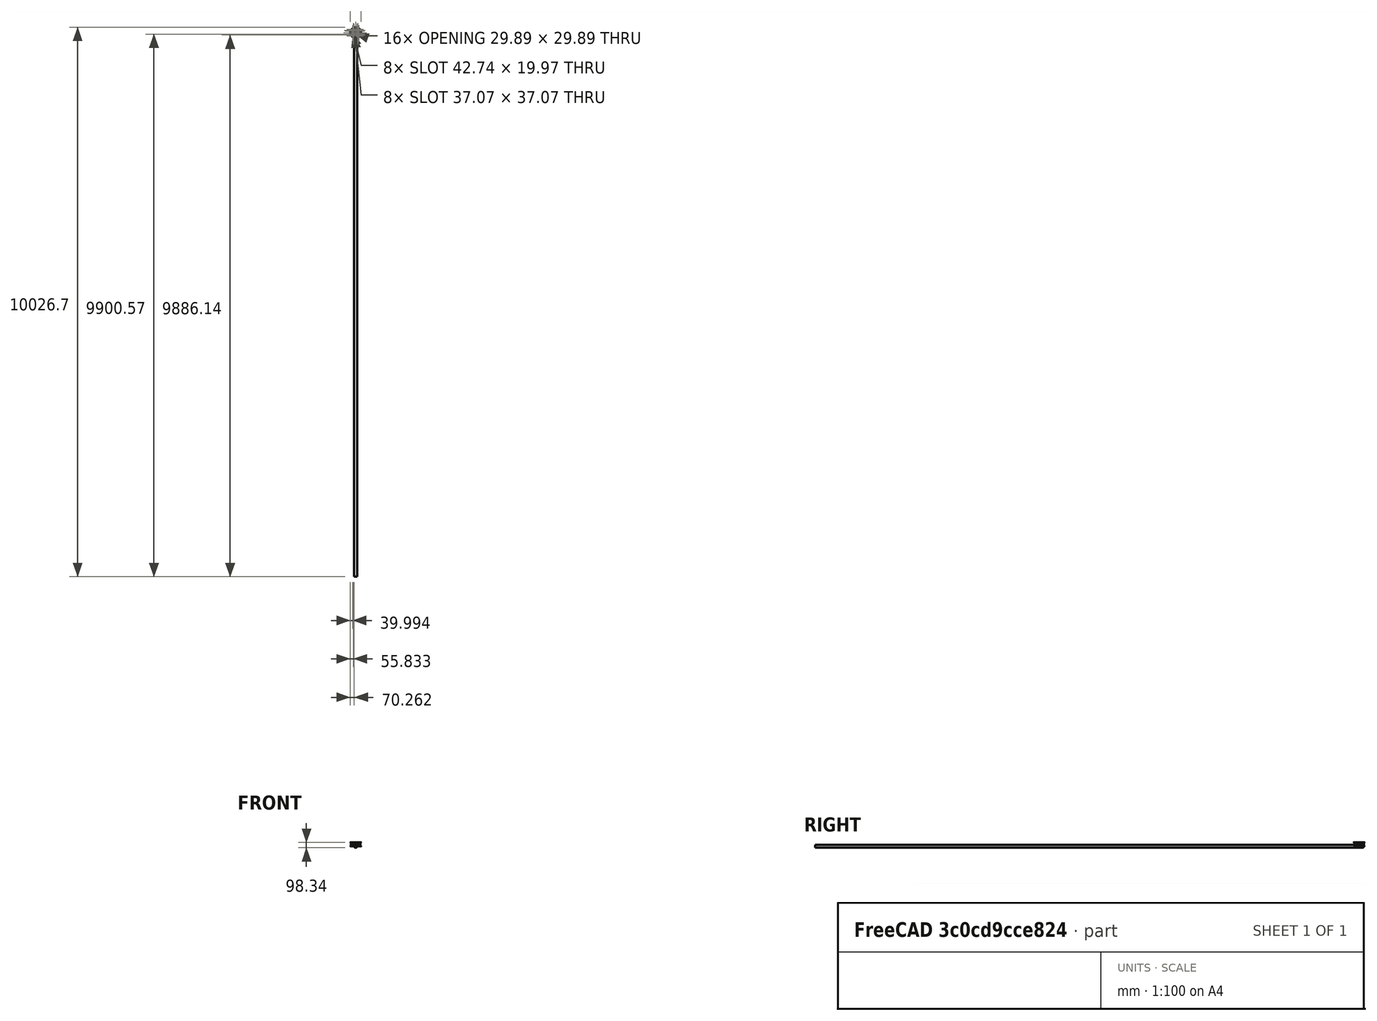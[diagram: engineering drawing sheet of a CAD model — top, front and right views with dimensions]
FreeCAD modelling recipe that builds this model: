
FCSTD DOCUMENT  (FreeCAD 0.14R3702 (Git))
Label: PLA-Reel
License: CC-BY 3.0
LicenseURL: http://creativecommons.org/licenses/by/3.0/
objects: Sketcher::SketchObject×7, PartDesign::Pocket×6, PartDesign::PolarPattern×5, Part::Extrusion×5, Part::Feature×3, Part::Part2DObjectPython×2, Part::MultiFuse×2, PartDesign::Revolution×1, Part::Cylinder×1, Part::Cut×1, Part::Torus×1, Part::FeaturePython×1, Part::Compound×1
note: 43 computed .brp shape members not serialized (recipe doc carries the construction recipe); baked Part::Feature solids carry a one-line shape summary decoded from their .brp

FEATURE [Sketcher::SketchObject] Sketch  label="main-body-sketch"
  Placement = pos=(0,0,0) rot=(1,0,0;1.5708rad)
  sketch-geometry (20):
    g0: LineSegment StartX=0 StartY=71.5 StartZ=0 EndX=97.185 EndY=71.5 EndZ=0
    g1: LineSegment StartX=97.185 StartY=0 StartZ=0 EndX=0 EndY=0 EndZ=0
    g2: LineSegment StartX=0 StartY=0 StartZ=0 EndX=0 EndY=71.5 EndZ=0
    g3: LineSegment [constr] StartX=0 StartY=35.75 StartZ=0 EndX=50.35 EndY=35.75 EndZ=0
    g4: LineSegment StartX=50.35 StartY=63.48 StartZ=0 EndX=50.35 EndY=8.02 EndZ=0
    g5: ArcOfCircle CenterX=97.185 CenterY=70.5 CenterZ=0 NormalX=0 NormalY=0 NormalZ=1 Radius=1 StartAngle=6.30999e-06 EndAngle=1.5708
    g6: LineSegment [constr] StartX=97.185 StartY=70.5 StartZ=0 EndX=98.185 EndY=70.5 EndZ=0
    g7: LineSegment [constr] StartX=97.185 StartY=71.5 StartZ=0 EndX=97.185 EndY=68.48 EndZ=0
    g8: ArcOfCircle CenterX=97.185 CenterY=69.48 CenterZ=0 NormalX=0 NormalY=0 NormalZ=1 Radius=1 StartAngle=4.71239 EndAngle=6.28319
    g9: LineSegment [constr] StartX=97.185 StartY=69.48 StartZ=0 EndX=98.185 EndY=69.48 EndZ=0
    g10: LineSegment StartX=98.185 StartY=70.5 StartZ=0 EndX=98.185 EndY=69.48 EndZ=0
    g11: ArcOfCircle CenterX=55.35 CenterY=63.48 CenterZ=0 NormalX=0 NormalY=0 NormalZ=1 Radius=5 StartAngle=1.5708 EndAngle=3.14159
    g12: LineSegment [constr] StartX=50.35 StartY=63.48 StartZ=0 EndX=55.35 EndY=63.48 EndZ=0
    g13: LineSegment [constr] StartX=55.35 StartY=68.48 StartZ=0 EndX=55.35 EndY=63.48 EndZ=0
    g14: LineSegment StartX=55.35 StartY=68.48 StartZ=0 EndX=97.185 EndY=68.48 EndZ=0
    g15: ArcOfCircle CenterX=55.35 CenterY=8.02 CenterZ=0 NormalX=0 NormalY=0 NormalZ=1 Radius=5 StartAngle=3.14159 EndAngle=4.71239
    g16: LineSegment StartX=55.35 StartY=3.02 StartZ=0 EndX=97.185 EndY=3.02 EndZ=0
    g17: ArcOfCircle CenterX=97.185 CenterY=2.02 CenterZ=0 NormalX=0 NormalY=0 NormalZ=1 Radius=1 StartAngle=0 EndAngle=1.5708
    g18: LineSegment StartX=98.185 StartY=2.02 StartZ=0 EndX=98.185 EndY=0.999994 EndZ=0
    g19: ArcOfCircle CenterX=97.185 CenterY=0.999994 CenterZ=0 NormalX=0 NormalY=0 NormalZ=1 Radius=0.999994 StartAngle=4.71238 EndAngle=6.28319
  constraints (58):
    c: Coincident(g1,g2)
    c: Coincident(g2,g0)
    c: Horizontal(g0)
    c: Horizontal(g1)
    c: Vertical(g2)
    c: Coincident(g1,g-1)
    c: DistanceY(g2) = 71.5
    c: DistanceX(g0) = 97.185
    c: Horizontal(g3)
    c: PointOnObject(g3,g2)
    c: Symmetric(g0,g-1,g3)
    c: Symmetric(g4,g4,g3)
    c: DistanceX(g3,g4) = 50.35
    c: Radius(g5) = 1
    c: Coincident(g5,g0)
    c: Horizontal(g6)
    c: Coincident(g6,g5)
    c: Vertical(g7)
    c: Coincident(g7,g0)
    c: PointOnObject(g5,g7)
    c: DistanceY(g7) = -3.02
    c: Equal(g8,g5)
    c: PointOnObject(g8,g7)
    c: Coincident(g8,g7)
    c: Horizontal(g9)
    c: Coincident(g9,g8)
    c: Coincident(g9,g8)
    c: Vertical(g10)
    c: Coincident(g10,g5)
    c: Coincident(g10,g8)
    c: Radius(g11) = 5
    c: Coincident(g11,g4)
    c: Horizontal(g12)
    c: Vertical(g13)
    c: Coincident(g13,g12)
    c: Coincident(g12,g11)
    c: Coincident(g12,g4)
    c: Coincident(g13,g11)
    c: Horizontal(g14)
    c: Coincident(g14,g11)
    c: Coincident(g14,g7)
    c: Symmetric(g1,g0,g3)
    c: PointOnObject(g3,g4)
    c: Coincident(g15,g4)
    c: Symmetric(g15,g11,g3)
    c: Symmetric(g15,g11,g3)
    c: Horizontal(g16)
    c: Coincident(g16,g15)
    c: Symmetric(g16,g7,g3)
    c: Coincident(g17,g16)
    c: Symmetric(g17,g8,g3)
    c: Symmetric(g17,g8,g3)
    c: Vertical(g18)
    c: Coincident(g18,g17)
    c: Symmetric(g18,g5,g3)
    c: Coincident(g19,g1)
    c: Coincident(g19,g18)
    c: Symmetric(g19,g6,g3)
FEATURE [PartDesign::Revolution] Revolution  label="main-body"
  Angle = 360
  Axis = (0,0,1)
  Base = (0,0,0)
  Placement = pos=(0,0,0) rot=(1,0,0;1.5708rad)
  ReferenceAxis = -> Sketch [V_Axis]
  Reversed = true
  Sketch = -> Sketch
FEATURE [Sketcher::SketchObject] Sketch001  label="axle-cutout-sketch"
  Placement = pos=(0,0,71.5) rot=(0,0,1;3.14159rad)
  Support = -> Revolution [Face2]
  sketch-geometry (1):
    g0: Circle CenterX=0 CenterY=0 CenterZ=0 NormalX=0 NormalY=0 NormalZ=1 Radius=26.84
  constraints (2):
    c: Coincident(g0,g-1)
    c: Radius(g0) = 26.84
FEATURE [PartDesign::Pocket] Pocket  label="axle-cutout"
  Length = 5
  Placement = pos=(0,0,0) rot=(1,0,0;1.5708rad)
  Sketch = -> Sketch001
  Type = 1
FEATURE [Sketcher::SketchObject] Sketch002  label="top-ring-1-cutout-master-sketch"
  ExternalGeometry = -> [Pocket]
  Placement = pos=(0,0,71.5) rot=(0,0,1;3.14159rad)
  Support = -> Pocket [Face5]
  sketch-geometry (16):
    g0: LineSegment [constr] StartX=-10.2712 StartY=24.7969 StartZ=0 EndX=0 EndY=0 EndZ=0
    g1: LineSegment StartX=-16.6608 StartY=43.0971 StartZ=0 EndX=-11.1788 EndY=29.8625 EndZ=0
    g2: ArcOfCircle [constr] CenterX=0 CenterY=0 CenterZ=0 NormalX=0 NormalY=0 NormalZ=1 Radius=29.13 StartAngle=1.5708 EndAngle=1.92572
    g3: LineSegment [constr] StartX=-11.1396 StartY=26.8934 StartZ=0 EndX=-10.1234 EndY=27.3144 EndZ=0
    g4: LineSegment [constr] StartX=-11.1788 StartY=29.8625 StartZ=0 EndX=-8.40719 EndY=31.0106 EndZ=0
    g5: LineSegment [constr] StartX=-8.40719 StartY=31.0106 StartZ=0 EndX=-7.62221 EndY=28.1151 EndZ=0
    g6: ArcOfCircle [constr] CenterX=0 CenterY=0 CenterZ=0 NormalX=0 NormalY=0 NormalZ=1 Radius=47.24 StartAngle=1.5708 EndAngle=1.94021
    g7: LineSegment [constr] StartX=-16.6608 StartY=43.0971 StartZ=0 EndX=-15.7369 EndY=43.4797 EndZ=0
    g8: LineSegment [constr] StartX=-16.0772 StartY=44.4201 StartZ=0 EndX=-15.7369 EndY=43.4797 EndZ=0
    g9: ArcOfCircle CenterX=-8.40719 CenterY=31.0106 CenterZ=0 NormalX=0 NormalY=0 NormalZ=1 Radius=3 StartAngle=3.53429 EndAngle=4.97713
    g10: ArcOfCircle CenterX=-15.7369 CenterY=43.4797 CenterZ=0 NormalX=0 NormalY=0 NormalZ=1 Radius=1 StartAngle=1.91806 EndAngle=3.53429
    g11: ArcOfCircle CenterX=0 CenterY=0 CenterZ=0 NormalX=0 NormalY=0 NormalZ=1 Radius=47.24 StartAngle=1.22353 EndAngle=1.91806
    g12: ArcOfCircle CenterX=0 CenterY=0 CenterZ=0 NormalX=0 NormalY=0 NormalZ=1 Radius=29.13 StartAngle=1.30605 EndAngle=1.83554
    g13: ArcOfCircle CenterX=15.7369 CenterY=43.4797 CenterZ=0 NormalX=0 NormalY=0 NormalZ=1 Radius=1 StartAngle=5.89049 EndAngle=7.50671
    g14: ArcOfCircle CenterX=8.40719 CenterY=31.0106 CenterZ=0 NormalX=0 NormalY=0 NormalZ=1 Radius=3 StartAngle=4.44765 EndAngle=5.89049
    g15: LineSegment StartX=16.6608 StartY=43.0971 StartZ=0 EndX=11.1788 EndY=29.8625 EndZ=0
  constraints (50):
    c: Coincident(g0,g-1)
    c: Angle(g-2,g0) = 0.392699
    c: PointOnObject(g0,g-3)
    c: Parallel(g1,g0)
    c: Coincident(g2,g-1)
    c: Radius(g2) = 29.13
    c: Perpendicular(g3,g0)
    c: PointOnObject(g3,g0)
    c: Distance(g3) = 1.1
    c: PointOnObject(g3,g1)
    c: Coincident(g2,g3)
    c: PointOnObject(g2,g-2)
    c: Coincident(g4,g1)
    c: Perpendicular(g4,g1)
    c: Coincident(g5,g4)
    c: Distance(g4) = 3
    c: Equal(g4,g5)
    c: Perpendicular(g5,g2)
    c: PointOnObject(g5,g2)
    c: Coincident(g6,g-1)
    c: Radius(g6) = 47.24
    c: PointOnObject(g6,g1)
    c: PointOnObject(g6,g-2)
    c: Perpendicular(g7,g1)
    c: Distance(g7) = 1
    c: Coincident(g7,g1)
    c: Equal(g8,g7)
    c: Coincident(g8,g7)
    c: Perpendicular(g8,g6)
    c: PointOnObject(g8,g6)
    c: Coincident(g9,g1)
    c: Coincident(g9,g5)
    c: Coincident(g9,g4)
    c: Coincident(g10,g1)
    c: Coincident(g10,g8)
    c: Coincident(g10,g7)
    c: Coincident(g11,g8)
    c: Symmetric(g11,g8,g-2)
    c: Coincident(g11,g-1)
    c: Coincident(g12,g5)
    c: Symmetric(g5,g12,g-2)
    c: Coincident(g12,g-1)
    c: Coincident(g13,g11)
    c: Symmetric(g13,g1,g-2)
    c: Symmetric(g13,g7,g-2)
    c: Coincident(g14,g12)
    c: Symmetric(g14,g1,g-2)
    c: Symmetric(g14,g4,g-2)
    c: Coincident(g15,g13)
    c: Coincident(g15,g14)
FEATURE [PartDesign::Pocket] Pocket001  label="top-ring-1-cutout-master"
  Length = 29.1
  Placement = pos=(0,0,0) rot=(1,0,0;1.5708rad)
  Sketch = -> Sketch002
  Type = 0
FEATURE [PartDesign::PolarPattern] PolarPattern  label="top-ring-1"
  Angle = 360
  Axis = -> Sketch002 [N_Axis]
  Occurrences = 8
  Originals = -> [Pocket001]
  Placement = pos=(0,0,0) rot=(1,0,0;1.5708rad)
FEATURE [Sketcher::SketchObject] Sketch003  label="top-ring-2-cutout-master"
  ExternalGeometry = -> [PolarPattern]
  Placement = pos=(0,0,71.5) rot=(0,0,1;3.14159rad)
  Support = -> PolarPattern [Face5]
  sketch-geometry (6):
    g0: LineSegment [constr] StartX=-10.2712 StartY=24.7969 StartZ=0 EndX=0 EndY=0 EndZ=0
    g1: LineSegment StartX=-21.3684 StartY=64.7449 StartZ=0 EndX=-14.5198 EndY=48.211 EndZ=0
    g2: LineSegment [constr] StartX=-10.2712 StartY=24.7969 StartZ=0 EndX=-5.61949 EndY=26.7237 EndZ=0
    g3: ArcOfCircle CenterX=0 CenterY=0 CenterZ=0 NormalX=0 NormalY=0 NormalZ=1 Radius=50.35 StartAngle=1.27826 EndAngle=1.86333
    g4: ArcOfCircle CenterX=0 CenterY=0 CenterZ=0 NormalX=0 NormalY=0 NormalZ=1 Radius=68.18 StartAngle=1.25201 EndAngle=1.88958
    g5: LineSegment StartX=21.3684 StartY=64.7449 StartZ=0 EndX=14.5198 EndY=48.211 EndZ=0
  constraints (19):
    c: Coincident(g0,g-1)
    c: Angle(g-2,g0) = 0.392699
    c: PointOnObject(g0,g-3)
    c: Parallel(g1,g0)
    c: PointOnObject(g2,g0)
    c: PointOnObject(g2,g1)
    c: Perpendicular(g2,g0)
    c: Distance(g2) = 5.035
    c: Coincident(g2,g0)
    c: Radius(g3) = 50.35
    c: Coincident(g3,g-1)
    c: Coincident(g3,g1)
    c: Symmetric(g1,g3,g-2)
    c: Radius(g4) = 68.18
    c: Coincident(g4,g-1)
    c: Coincident(g1,g4)
    c: Symmetric(g1,g4,g-2)
    c: Coincident(g5,g3)
    c: Coincident(g5,g4)
FEATURE [PartDesign::Pocket] Pocket002  label="top-ring-2-cutout"
  Length = 1
  Placement = pos=(0,0,0) rot=(1,0,0;1.5708rad)
  Sketch = -> Sketch003
  Type = 0
FEATURE [PartDesign::PolarPattern] PolarPattern001  label="top-ring-2"
  Angle = 360
  Axis = -> Sketch003 [N_Axis]
  Occurrences = 8
  Originals = -> [Pocket002]
  Placement = pos=(0,0,0) rot=(1,0,0;1.5708rad)
FEATURE [Sketcher::SketchObject] Sketch004  label="bottom-ring-1-cutout-master-sketch"
  ExternalGeometry = -> [PolarPattern001]
  Placement = pos=(0,0,0) rot=(1,0,0;3.14159rad)
  Support = -> PolarPattern001 [Face1]
  sketch-geometry (16):
    g0: LineSegment [constr] StartX=-10.2712 StartY=24.7969 StartZ=0 EndX=0 EndY=0 EndZ=0
    g1: LineSegment StartX=-16.6608 StartY=43.0971 StartZ=0 EndX=-11.1788 EndY=29.8625 EndZ=0
    g2: LineSegment [constr] StartX=-10.2712 StartY=24.7969 StartZ=0 EndX=-9.25496 EndY=25.2179 EndZ=0
    g3: ArcOfCircle [constr] CenterX=0 CenterY=0 CenterZ=0 NormalX=0 NormalY=0 NormalZ=1 Radius=29.13 StartAngle=1.5708 EndAngle=1.9635
    g4: LineSegment [constr] StartX=-11.1788 StartY=29.8625 StartZ=0 EndX=-8.40719 EndY=31.0106 EndZ=0
    g5: LineSegment [constr] StartX=-8.40719 StartY=31.0106 StartZ=0 EndX=-7.62221 EndY=28.1151 EndZ=0
    g6: ArcOfCircle CenterX=-8.40719 CenterY=31.0106 CenterZ=0 NormalX=0 NormalY=0 NormalZ=1 Radius=3 StartAngle=3.53429 EndAngle=4.97713
    g7: ArcOfCircle [constr] CenterX=0 CenterY=0 CenterZ=0 NormalX=0 NormalY=0 NormalZ=1 Radius=47.24 StartAngle=1.5708 EndAngle=1.94021
    g8: LineSegment [constr] StartX=-16.6608 StartY=43.0971 StartZ=0 EndX=-15.7369 EndY=43.4797 EndZ=0
    g9: LineSegment [constr] StartX=-16.0772 StartY=44.4201 StartZ=0 EndX=-15.7369 EndY=43.4797 EndZ=0
    g10: ArcOfCircle CenterX=-15.7369 CenterY=43.4797 CenterZ=0 NormalX=0 NormalY=0 NormalZ=1 Radius=1 StartAngle=1.91806 EndAngle=3.53429
    g11: ArcOfCircle CenterX=0 CenterY=0 CenterZ=0 NormalX=0 NormalY=0 NormalZ=1 Radius=47.24 StartAngle=1.22353 EndAngle=1.91806
    g12: ArcOfCircle CenterX=0 CenterY=0 CenterZ=0 NormalX=0 NormalY=0 NormalZ=1 Radius=29.13 StartAngle=1.30605 EndAngle=1.83554
    g13: ArcOfCircle CenterX=15.7369 CenterY=43.4797 CenterZ=0 NormalX=0 NormalY=0 NormalZ=1 Radius=1 StartAngle=5.89049 EndAngle=7.50671
    g14: ArcOfCircle CenterX=8.40719 CenterY=31.0106 CenterZ=0 NormalX=0 NormalY=0 NormalZ=1 Radius=3 StartAngle=4.44765 EndAngle=5.89049
    g15: LineSegment StartX=16.6608 StartY=43.0971 StartZ=0 EndX=11.1788 EndY=29.8625 EndZ=0
  constraints (50):
    c: Coincident(g0,g-1)
    c: PointOnObject(g0,g-3)
    c: Angle(g-2,g0) = 0.392699
    c: Parallel(g1,g0)
    c: Coincident(g2,g0)
    c: Perpendicular(g2,g0)
    c: Distance(g2) = 1.1
    c: PointOnObject(g2,g1)
    c: Coincident(g3,g-1)
    c: Radius(g3) = 29.13
    c: PointOnObject(g3,g-2)
    c: PointOnObject(g3,g0)
    c: Perpendicular(g1,g4)
    c: Coincident(g4,g1)
    c: Distance(g4) = 3
    c: Coincident(g5,g4)
    c: Equal(g4,g5)
    c: Perpendicular(g5,g3)
    c: PointOnObject(g5,g3)
    c: Coincident(g6,g1)
    c: Coincident(g5,g6)
    c: Coincident(g6,g4)
    c: Radius(g7) = 47.24
    c: Coincident(g7,g-1)
    c: PointOnObject(g7,g-2)
    c: PointOnObject(g7,g1)
    c: Perpendicular(g8,g1)
    c: Distance(g8) = 1
    c: Coincident(g8,g1)
    c: Coincident(g9,g8)
    c: Equal(g8,g9)
    c: Perpendicular(g9,g7)
    c: PointOnObject(g9,g7)
    c: Coincident(g10,g1)
    c: Coincident(g10,g9)
    c: Coincident(g10,g8)
    c: Coincident(g11,g-1)
    c: Coincident(g11,g9)
    c: Symmetric(g11,g9,g-2)
    c: Coincident(g12,g5)
    c: Symmetric(g5,g12,g-2)
    c: Coincident(g12,g-1)
    c: Coincident(g13,g11)
    c: Symmetric(g13,g1,g-2)
    c: Symmetric(g13,g8,g-2)
    c: Coincident(g14,g12)
    c: Symmetric(g14,g1,g-2)
    c: Symmetric(g4,g14,g-2)
    c: Coincident(g15,g13)
    c: Coincident(g15,g14)
FEATURE [PartDesign::Pocket] Pocket003  label="bottom-ring-1-cutout-master"
  Length = 39.63
  Placement = pos=(0,0,0) rot=(1,0,0;1.5708rad)
  Sketch = -> Sketch004
  Type = 0
FEATURE [PartDesign::PolarPattern] PolarPattern002  label="bottom-ring-1-cutout"
  Angle = 360
  Axis = -> Sketch004 [N_Axis]
  Occurrences = 8
  Originals = -> [Pocket003]
  Placement = pos=(0,0,0) rot=(1,0,0;1.5708rad)
FEATURE [Sketcher::SketchObject] Sketch005  label="bottom-ring-2-cutout-master"
  ExternalGeometry = -> [PolarPattern002]
  Placement = pos=(0,0,0) rot=(1,0,0;3.14159rad)
  Support = -> PolarPattern002 [Face1]
  sketch-geometry (6):
    g0: LineSegment [constr] StartX=-10.2712 StartY=24.7969 StartZ=0 EndX=0 EndY=0 EndZ=0
    g1: LineSegment StartX=-26.4467 StartY=77.0051 StartZ=0 EndX=-14.5198 EndY=48.211 EndZ=0
    g2: LineSegment [constr] StartX=-10.2712 StartY=24.7969 StartZ=0 EndX=-5.61949 EndY=26.7237 EndZ=0
    g3: ArcOfCircle CenterX=0 CenterY=0 CenterZ=0 NormalX=0 NormalY=0 NormalZ=1 Radius=50.35 StartAngle=1.27826 EndAngle=1.86333
    g4: ArcOfCircle CenterX=0 CenterY=0 CenterZ=0 NormalX=0 NormalY=0 NormalZ=1 Radius=81.42 StartAngle=1.23998 EndAngle=1.90162
    g5: LineSegment StartX=26.4467 StartY=77.0051 StartZ=0 EndX=14.5198 EndY=48.211 EndZ=0
  constraints (18):
    c: Coincident(g0,g-1)
    c: PointOnObject(g0,g-3)
    c: Angle(g-2,g0) = 0.392699
    c: Parallel(g1,g0)
    c: Coincident(g2,g0)
    c: Perpendicular(g2,g0)
    c: PointOnObject(g2,g1)
    c: Distance(g2) = 5.035
    c: Radius(g3) = 50.35
    c: Coincident(g3,g1)
    c: Symmetric(g1,g3,g-2)
    c: Coincident(g3,g-1)
    c: Symmetric(g4,g4,g-2)
    c: Coincident(g4,g1)
    c: Radius(g4) = 81.42
    c: Coincident(g4,g-1)
    c: Coincident(g5,g4)
    c: Coincident(g5,g3)
FEATURE [PartDesign::Pocket] Pocket004  label="bottom-ring-2-cutout-master001"
  Length = 1
  Placement = pos=(0,0,0) rot=(1,0,0;1.5708rad)
  Sketch = -> Sketch005
  Type = 0
FEATURE [PartDesign::PolarPattern] PolarPattern003  label="bottom-ring-2-cutout"
  Angle = 360
  Axis = -> Sketch005 [N_Axis]
  Occurrences = 8
  Originals = -> [Pocket004]
  Placement = pos=(0,0,0) rot=(1,0,0;1.5708rad)
FEATURE [Sketcher::SketchObject] Sketch006
  Placement = pos=(0,0,0) rot=(1,0,0;3.14159rad)
  Support = -> PolarPattern003 [Face1]
  sketch-geometry (2):
    g0: Circle CenterX=-10.07 CenterY=-86.54 CenterZ=0 NormalX=0 NormalY=0 NormalZ=1 Radius=2
    g1: Circle CenterX=10.07 CenterY=-86.54 CenterZ=0 NormalX=0 NormalY=0 NormalZ=1 Radius=2
  constraints (5):
    c: Radius(g0) = 2
    c: Equal(g1,g0)
    c: Symmetric(g0,g1,g-2)
    c: DistanceY(g-1,g0) = -86.54
    c: DistanceX(g-1,g0) = -10.07
FEATURE [PartDesign::Pocket] Pocket005  label="bottom-drills-master"
  Length = 5
  Placement = pos=(0,0,0) rot=(1,0,0;1.5708rad)
  Sketch = -> Sketch006
  Type = 0
FEATURE [PartDesign::PolarPattern] PolarPattern004  label="bottom-drills"
  Angle = 360
  Axis = -> Sketch006 [N_Axis]
  Occurrences = 4
  Originals = -> [Pocket005]
  Placement = pos=(0,0,0) rot=(1,0,0;1.5708rad)
FEATURE [Part::Cylinder] Cylinder  label="init-hole-cylinder"
  Angle = 360
  Height = 20
  Placement = pos=(29.7494,42.6775,63.392) rot=(0.139286,-0.700214,0.700214;3.41838rad)
  Radius = 2
FEATURE [Part::Part2DObjectPython] ShapeString001  label="PS-face"  # Draft 2D object (typed FeaturePython)
  FontFile = <path>
  Placement = pos=(-3.33298,-63.3113,1) rot=(1,0,0;3.14159rad)
  Size = 1.8
  String = PS
  Tracking = 0
FEATURE [Part::Part2DObjectPython] ShapeString  label="06-face"  # Draft 2D object (typed FeaturePython)
  FontFile = <path>
  Placement = pos=(-2.58493,-71.1244,1) rot=(1,0,0;3.14159rad)
  Size = 1.8
  String = 6
  Tracking = 0
FEATURE [Part::Feature] Face  label="arrow-1-face"
  shape: bbox 5.405 x 6.172 x 2e-07 mm, 1 faces, 0 solids (baked)
FEATURE [Part::Extrusion] Extrude  label="arrow-1"
  Base = -> Face
  Dir = (0,0,0.15)
  Solid = true
FEATURE [Part::Feature] Face001  label="arrow-2-face"
  shape: bbox 7.293 x 4.281 x 2e-07 mm, 1 faces, 0 solids (baked)
FEATURE [Part::Extrusion] Extrude001  label="arrow-2"
  Base = -> Face001
  Dir = (0,0,0.15)
  Placement = pos=(0,0,-0.15) rot=(0,0,1;0rad)
  Solid = true
FEATURE [Part::Feature] Face002  label="arrow-3-face"
  shape: bbox 5.571 x 6.782 x 2e-07 mm, 1 faces, 0 solids (baked)
FEATURE [Part::Extrusion] Extrude002  label="arrow-3"
  Base = -> Face002
  Dir = (0,0,0.15)
  Placement = pos=(0,0,-0.15) rot=(0,0,1;0rad)
  Solid = true
FEATURE [Part::Extrusion] Extrude003  label="ps"
  Base = -> ShapeString001
  Dir = (0,0,0.15)
  Placement = pos=(0,0,-0.15) rot=(0,0,1;0rad)
  Solid = true
FEATURE [Part::Extrusion] Extrude004  label="06"
  Base = -> ShapeString
  Dir = (0,0,0.15)
  Placement = pos=(0,0,-0.15) rot=(0,0,1;0rad)
  Solid = true
FEATURE [Part::MultiFuse] Fusion  label="recicle"
  Shapes = -> [Extrude,Extrude001,Extrude002,Extrude003,Extrude004]
FEATURE [Part::Cut] Cut
  Base = -> PolarPattern004
  Tool = -> Cylinder
FEATURE [Part::MultiFuse] Fusion001  label="PLA-reel"
  Shapes = -> [Cut,Fusion]
FEATURE [Part::Torus] Torus
  Angle1 = -180
  Angle2 = 180
  Angle3 = 360
  Placement = pos=(0,0,4) rot=(0,0,1;0rad)
  Radius1 = 85
  Radius2 = 0.9
FEATURE [Part::FeaturePython] Array  label="PLA"  # Draft array (typed FeaturePython)
  Angle = 360
  ArrayType = 0
  Axis = (0,0,1)
  Base = -> Torus
  Center = (0,0,0)
  IntervalX = (1,0,0)
  IntervalY = (0,1,0)
  IntervalZ = (0,0,1.8)
  NumberPolar = 1
  NumberX = 1
  NumberY = 1
  NumberZ = 36
FEATURE [Part::Compound] Compound  label="reel+pla"
  Links = -> [Fusion001,Array]
note: 2 file-system paths scrubbed to <path> (originals preserved in the JSON sidecar)
